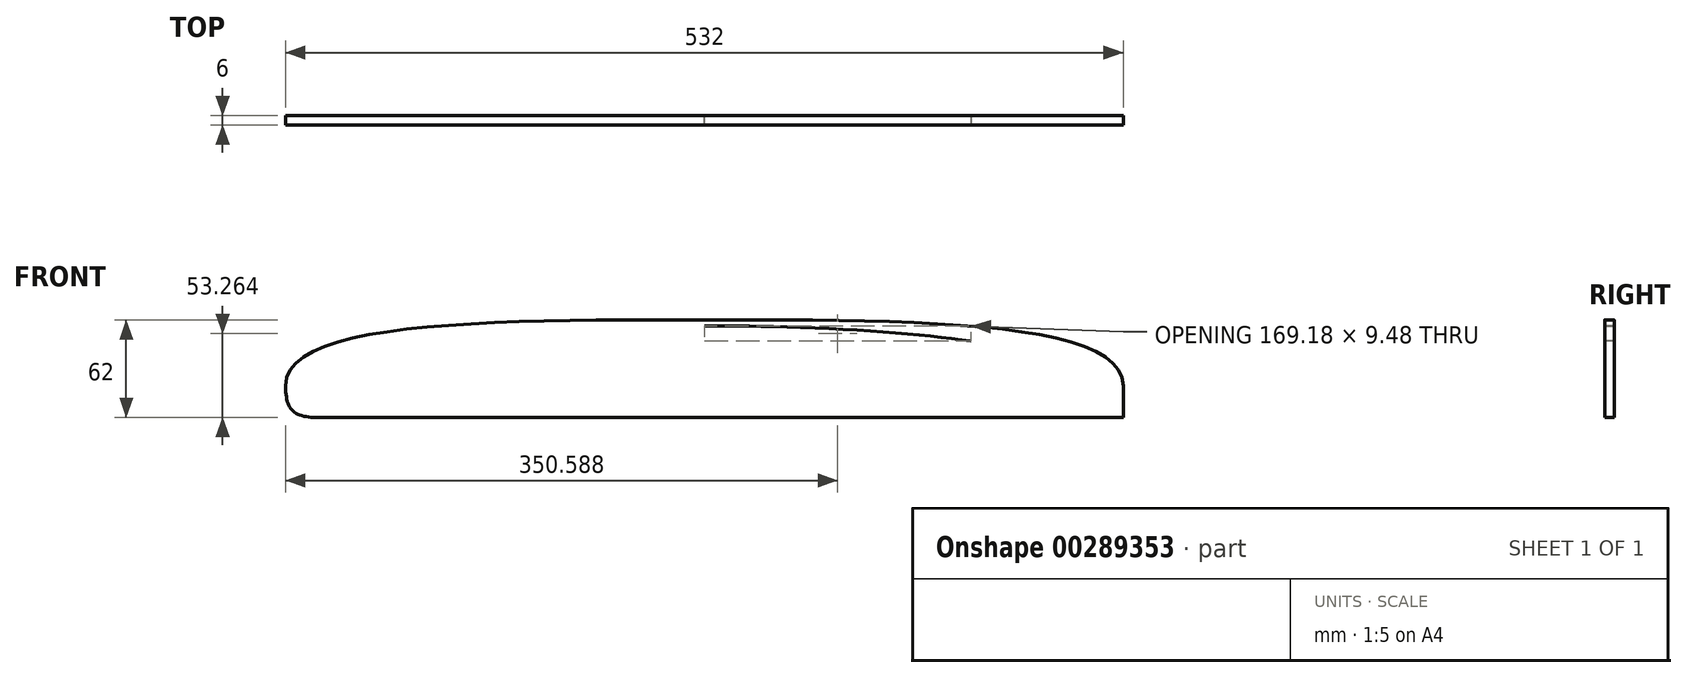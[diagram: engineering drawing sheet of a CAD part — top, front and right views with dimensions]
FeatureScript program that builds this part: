
annotation { "Feature Type Name" : "Feature", "Feature Type Description" : "" }
export const myFeature = defineFeature(function(context is Context, id is Id, definition is map)
    precondition{}
    {
        {
            var Q0;
            Q0=qCreatedBy(makeId("Front.planeOp"),FACE);
            var sketch = newSketch(context, id + "F0", { "sketchPlane" : qUnion([Q0])});
            skLineSegment(sketch, "E0.bottom", {"start": v(0, 0) * mm, "end": v(264, 0) * mm, "construction": true});
            skLineSegment(sketch, "E0.top", {"start": v(0, 62) * mm, "end": v(266, 62) * mm, "construction": true});
            skLineSegment(sketch, "E0.left", {"start": v(0, 0) * mm, "end": v(0, 62) * mm, "construction": true});
            skLineSegment(sketch, "E0.right", {"start": v(266, 6) * mm, "end": v(266, 62) * mm, "construction": true});
            skPoint(sketch, "E1", {"position": v(266, 20) * mm});
            skFitSpline(sketch, "E2", {"points": [v(0, 62) * mm, v(266, 20) * mm], "startDerivative": vector(399, 0) * mm, "endDerivative": vector(0, -126) * mm});
            skLineSegment(sketch, "E3", {"start": v(246, 0) * mm, "end": v(0, 0) * mm});
            skFitSpline(sketch, "E4.MirrorCS", {"points": [v(0, 62) * mm, v(-266, 20) * mm], "startDerivative": vector(-399, 0) * mm, "endDerivative": vector(0, -126) * mm});
            skFitSpline(sketch, "E5.MirrorCS", {"points": [v(-266, 20) * mm, v(-246, 0) * mm], "startDerivative": vector(0, -45) * mm, "endDerivative": vector(45, 0) * mm});
            skLineSegment(sketch, "E6.MirrorCS", {"start": v(-246, 0) * mm, "end": v(0, 0) * mm});
            skLineSegment(sketch, "E7", {"start": v(246, 0) * mm, "end": v(264, 0) * mm});
            skLineSegment(sketch, "E8", {"start": v(266, 6) * mm, "end": v(266, 20) * mm});
            skPoint(sketch, "E9.orphan", {"position": v(266, 0) * mm});
            skLineSegment(sketch, "E10", {"start": v(264, 0) * mm, "end": v(266, 0) * mm});
            skLineSegment(sketch, "E11", {"start": v(266, 6) * mm, "end": v(266, 0) * mm});
            skLineSegment(sketch, "E12", {"start": v(0, 70) * mm, "end": v(270, 70) * mm, "construction": true});
            skLineSegment(sketch, "E13", {"start": v(270, 70) * mm, "end": v(270, 0) * mm, "construction": true});
            skLineSegment(sketch, "E14", {"start": v(270, 0) * mm, "end": v(0, 0) * mm, "construction": true});
            skSolve(sketch);
        }
        {
            var Q0;
            Q0 = qSketchRegion(id + "F0", true);
            extrude(context, id + "F1", {"entities" : qUnion([Q0]), "depth" : 6 * mm});
        }
        {
            var Q0;
            Q0=makeQuery(id+"F1.opExtrude","CAP_FACE",FACE,{"disambiguationData":[OSD([sQuery(id+"F0.wireOp",EDGE,"E2"),sQuery(id+"F0.wireOp",EDGE,"E3"),sQuery(id+"F0.wireOp",EDGE,"E4.MirrorCS"),sQuery(id+"F0.wireOp",EDGE,"E5.MirrorCS"),sQuery(id+"F0.wireOp",EDGE,"E6.MirrorCS"),sQuery(id+"F0.wireOp",EDGE,"E7"),sQuery(id+"F0.wireOp",EDGE,"E8"),sQuery(id+"F0.wireOp",EDGE,"l2RiLHSC-aDhs-CfYt-97Ve-NNkehFv2K1TW.top"),sQuery(id+"F0.wireOp",EDGE,"l2RiLHSC-aDhs-CfYt-97Ve-NNkehFv2K1TW.left")])],"isStart":false});
            var sketch = newSketch(context, id + "F2", { "sketchPlane" : qUnion([Q0])});
            skLineSegment(sketch, "E15", {"start": v(0, 0) * mm, "end": v(0, 150.42) * mm, "construction": true});
            skFitSpline(sketch, "E16.0", {"points": [v(0, 58) * mm, v(16.76, 58) * mm, v(50.29, 57.53) * mm, v(98.94, 55.38) * mm, v(136.78, 52.34) * mm, v(164.59, 49.13) * mm, v(184, 46.34) * mm, v(201.75, 43.17) * mm, v(217.6, 39.62) * mm, v(231.29, 35.73) * mm, v(240.66, 32.26) * mm, v(246.76, 29.43) * mm, v(250.59, 27.32) * mm, v(253.61, 25.3) * mm, v(255.8, 23.45) * mm, v(256.94, 22.17) * mm, v(257.49, 21.38) * mm, v(257.75, 20.92) * mm, v(257.9, 20.58) * mm, v(257.96, 20.34) * mm, v(258, 20.17) * mm, v(258, 20.06) * mm, v(258, 20) * mm]});
            skLineSegment(sketch, "E17", {"start": v(25, 12) * mm, "end": v(75, 12) * mm});
            skLineSegment(sketch, "E18", {"start": v(259.27, 17) * mm, "end": v(259.27, 22.15) * mm});
            skLineSegment(sketch, "E19", {"start": v(20, 44.99) * mm, "end": v(20, 17) * mm});
            skLineSegment(sketch, "E20", {"start": v(80, 44.7) * mm, "end": v(80, 17) * mm});
            skLineSegment(sketch, "E21", {"start": v(100, 43.98) * mm, "end": v(100, 17) * mm});
            skLineSegment(sketch, "E22", {"start": v(160, 42.03) * mm, "end": v(160, 17) * mm});
            skLineSegment(sketch, "E23", {"start": v(180, 39.42) * mm, "end": v(180, 17) * mm});
            skLineSegment(sketch, "E24.trimOffspring", {"start": v(105, 12) * mm, "end": v(155, 12) * mm});
            skFitSpline(sketch, "E25.trimOffspring", {"points": [v(0, 58) * mm, v(16.76, 58) * mm, v(50.29, 57.53) * mm, v(98.94, 55.38) * mm, v(136.78, 52.34) * mm, v(164.59, 49.13) * mm, v(184, 46.34) * mm, v(201.75, 43.17) * mm, v(217.6, 39.62) * mm, v(231.29, 35.73) * mm, v(240.66, 32.26) * mm, v(246.76, 29.43) * mm, v(250.59, 27.32) * mm, v(253.61, 25.3) * mm, v(255.8, 23.45) * mm, v(256.94, 22.17) * mm, v(257.49, 21.38) * mm, v(257.75, 20.92) * mm, v(257.9, 20.58) * mm, v(257.96, 20.34) * mm, v(258, 20.17) * mm, v(258, 20.06) * mm, v(258, 20) * mm]});
            skFitSpline(sketch, "E26.trimOffspring", {"points": [v(0, 58) * mm, v(16.76, 58) * mm, v(50.29, 57.53) * mm, v(98.94, 55.38) * mm, v(136.78, 52.34) * mm, v(164.59, 49.13) * mm, v(184, 46.34) * mm, v(201.75, 43.17) * mm, v(217.6, 39.62) * mm, v(231.29, 35.73) * mm, v(240.66, 32.26) * mm, v(246.76, 29.43) * mm, v(250.59, 27.32) * mm, v(253.61, 25.3) * mm, v(255.8, 23.45) * mm, v(256.94, 22.17) * mm, v(257.49, 21.38) * mm, v(257.75, 20.92) * mm, v(257.9, 20.58) * mm, v(257.96, 20.34) * mm, v(258, 20.17) * mm, v(258, 20.06) * mm, v(258, 20) * mm]});
            skLineSegment(sketch, "E27.trimOffspring", {"start": v(185, 12) * mm, "end": v(254.27, 12) * mm});
            skPoint(sketch, "E28.visualSharp", {"position": v(20, 50) * mm});
            skArc(sketch, "E28.filletArc", {"start": v(25, 49.99) * mm, "mid": v(21.47, 48.53) * mm, "end": v(20, 44.99) * mm});
            skPoint(sketch, "E29.visualSharp", {"position": v(80, 49.65) * mm});
            skArc(sketch, "E29.filletArc", {"start": v(80, 44.7) * mm, "mid": v(78.56, 48.22) * mm, "end": v(75.06, 49.7) * mm});
            skPoint(sketch, "E30.visualSharp", {"position": v(80, 12) * mm});
            skArc(sketch, "E30.filletArc", {"start": v(75, 12) * mm, "mid": v(78.54, 13.46) * mm, "end": v(80, 17) * mm});
            skPoint(sketch, "E31.visualSharp", {"position": v(20, 12) * mm});
            skArc(sketch, "E31.filletArc", {"start": v(20, 17) * mm, "mid": v(21.46, 13.46) * mm, "end": v(25, 12) * mm});
            skPoint(sketch, "E32.visualSharp", {"position": v(100, 12) * mm});
            skArc(sketch, "E32.filletArc", {"start": v(100, 17) * mm, "mid": v(101.46, 13.46) * mm, "end": v(105, 12) * mm});
            skPoint(sketch, "E33.visualSharp", {"position": v(100, 49.05) * mm});
            skArc(sketch, "E33.filletArc", {"start": v(105.08, 48.97) * mm, "mid": v(101.5, 47.54) * mm, "end": v(100, 43.98) * mm});
            skPoint(sketch, "E34.visualSharp", {"position": v(160, 46.7) * mm});
            skArc(sketch, "E34.filletArc", {"start": v(160, 42.03) * mm, "mid": v(158.65, 45.45) * mm, "end": v(155.33, 47.02) * mm});
            skPoint(sketch, "E35.visualSharp", {"position": v(160, 12) * mm});
            skArc(sketch, "E35.filletArc", {"start": v(155, 12) * mm, "mid": v(158.54, 13.46) * mm, "end": v(160, 17) * mm});
            skPoint(sketch, "E36.visualSharp", {"position": v(180, 12) * mm});
            skArc(sketch, "E36.filletArc", {"start": v(180, 17) * mm, "mid": v(181.46, 13.46) * mm, "end": v(185, 12) * mm});
            skPoint(sketch, "E37.visualSharp", {"position": v(180, 44.98) * mm});
            skArc(sketch, "E37.filletArc", {"start": v(185.56, 44.4) * mm, "mid": v(181.67, 43.15) * mm, "end": v(180, 39.42) * mm});
            skPoint(sketch, "E38.visualSharp", {"position": v(259.27, 12) * mm});
            skArc(sketch, "E38.filletArc", {"start": v(254.27, 12) * mm, "mid": v(257.8, 13.46) * mm, "end": v(259.27, 17) * mm});
            skSolve(sketch);
        }
        {
            var Q0;
            Q0 = qSketchRegion(id + "F2", true);
            extrude(context, id + "F3", {"entities" : qUnion([Q0]), "operationType" : NewBodyOperationType.REMOVE, "oppositeDirection" : true, "depth" : 25 * mm});
        }
    });
